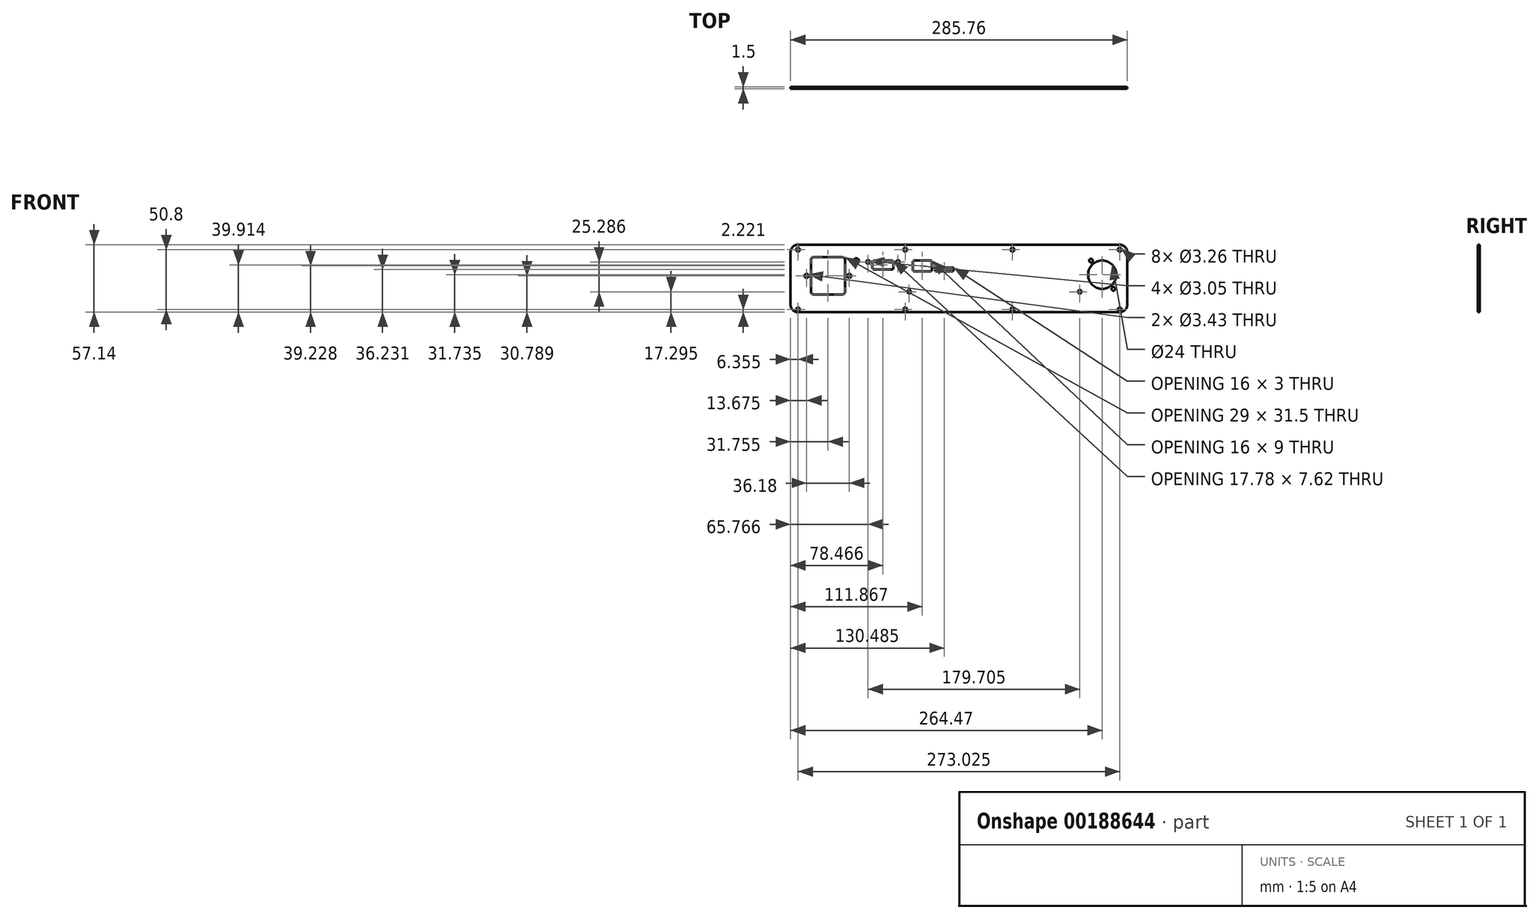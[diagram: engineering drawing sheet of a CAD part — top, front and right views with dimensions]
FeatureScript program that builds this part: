
annotation { "Feature Type Name" : "Feature", "Feature Type Description" : "" }
export const myFeature = defineFeature(function(context is Context, id is Id, definition is map)
    precondition{}
    {
        {
            var Q0;
            Q0=qCreatedBy(makeId("Front.planeOp"),FACE);
            var sketch = newSketch(context, id + "F0", { "sketchPlane" : qUnion([Q0])});
            skLineSegment(sketch, "E0", {"start": v(136.53, 28.58) * mm, "end": v(-136.53, 28.58) * mm});
            skArc(sketch, "E1", {"start": v(-136.53, 28.58) * mm, "mid": v(-141.02, 26.72) * mm, "end": v(-142.88, 22.23) * mm});
            skLineSegment(sketch, "E2", {"start": v(-142.88, 22.23) * mm, "end": v(-142.88, -22.23) * mm});
            skArc(sketch, "E3", {"start": v(-142.88, -22.23) * mm, "mid": v(-141.02, -26.72) * mm, "end": v(-136.53, -28.58) * mm});
            skLineSegment(sketch, "E4", {"start": v(-136.53, -28.58) * mm, "end": v(136.53, -28.58) * mm});
            skArc(sketch, "E5", {"start": v(136.53, -28.58) * mm, "mid": v(141.02, -26.72) * mm, "end": v(142.88, -22.23) * mm});
            skLineSegment(sketch, "E6", {"start": v(142.88, -22.23) * mm, "end": v(142.88, 22.23) * mm});
            skArc(sketch, "E7", {"start": v(142.88, 22.23) * mm, "mid": v(141.02, 26.72) * mm, "end": v(136.53, 28.58) * mm});
            skCircle(sketch, "E8", {"center": v(-87.1, 14.8) * mm, "radius": 2.29 * mm});
            skCircle(sketch, "E9", {"center": v(-42.19, -11.28) * mm, "radius": 1.52 * mm});
            skCircle(sketch, "E10", {"center": v(102.6, -11.28) * mm, "radius": 1.52 * mm});
            skLineSegment(sketch, "E11", {"start": v(-4.4, 8.27) * mm, "end": v(-4.4, 7.05) * mm});
            skArc(sketch, "E12", {"start": v(-5.28, 6.16) * mm, "mid": v(-4.66, 6.42) * mm, "end": v(-4.4, 7.05) * mm});
            skLineSegment(sketch, "E13", {"start": v(-5.28, 6.16) * mm, "end": v(-19.5, 6.16) * mm});
            skArc(sketch, "E14", {"start": v(-20.4, 7.05) * mm, "mid": v(-20.13, 6.42) * mm, "end": v(-19.5, 6.16) * mm});
            skLineSegment(sketch, "E15", {"start": v(-20.4, 7.05) * mm, "end": v(-20.4, 8.27) * mm});
            skArc(sketch, "E16", {"start": v(-19.5, 9.16) * mm, "mid": v(-20.13, 8.9) * mm, "end": v(-20.4, 8.27) * mm});
            skLineSegment(sketch, "E17", {"start": v(-19.5, 9.16) * mm, "end": v(-5.28, 9.16) * mm});
            skArc(sketch, "E18", {"start": v(-4.4, 8.27) * mm, "mid": v(-4.66, 8.9) * mm, "end": v(-5.28, 9.16) * mm});
            skCircle(sketch, "E19", {"center": v(-77.11, 14.01) * mm, "radius": 1.52 * mm});
            skCircle(sketch, "E20", {"center": v(-51.71, 14.01) * mm, "radius": 1.52 * mm});
            skCircle(sketch, "E21", {"center": v(121.6, 3.17) * mm, "radius": 12 * mm});
            skCircle(sketch, "E22", {"center": v(112.12, 15.15) * mm, "radius": 1.55 * mm});
            skCircle(sketch, "E23", {"center": v(131.12, -8.85) * mm, "radius": 1.55 * mm});
            skCircle(sketch, "E24", {"center": v(-129.2, 2.22) * mm, "radius": 1.71 * mm});
            skLineSegment(sketch, "E25", {"start": v(-96.62, 15.97) * mm, "end": v(-96.62, -11.53) * mm});
            skArc(sketch, "E26", {"start": v(-98.62, -13.53) * mm, "mid": v(-97.21, -12.95) * mm, "end": v(-96.62, -11.53) * mm});
            skLineSegment(sketch, "E27", {"start": v(-98.62, -13.53) * mm, "end": v(-123.63, -13.53) * mm});
            skArc(sketch, "E28", {"start": v(-125.63, -11.53) * mm, "mid": v(-125.04, -12.95) * mm, "end": v(-123.63, -13.53) * mm});
            skLineSegment(sketch, "E29", {"start": v(-125.63, -11.53) * mm, "end": v(-125.63, 15.97) * mm});
            skArc(sketch, "E30", {"start": v(-123.63, 17.97) * mm, "mid": v(-125.04, 17.38) * mm, "end": v(-125.63, 15.97) * mm});
            skLineSegment(sketch, "E31", {"start": v(-123.63, 17.97) * mm, "end": v(-98.62, 17.97) * mm});
            skArc(sketch, "E32", {"start": v(-96.62, 15.97) * mm, "mid": v(-97.21, 17.38) * mm, "end": v(-98.62, 17.97) * mm});
            skCircle(sketch, "E33", {"center": v(-93.02, 2.22) * mm, "radius": 1.71 * mm});
            skCircle(sketch, "E34", {"center": v(-136.53, 24.45) * mm, "radius": 1.63 * mm});
            skCircle(sketch, "E35", {"center": v(-136.53, -26.35) * mm, "radius": 1.63 * mm});
            skCircle(sketch, "E36", {"center": v(-45.52, 24.45) * mm, "radius": 1.63 * mm});
            skCircle(sketch, "E37", {"center": v(-45.52, -26.35) * mm, "radius": 1.63 * mm});
            skCircle(sketch, "E38", {"center": v(45.5, 24.45) * mm, "radius": 1.63 * mm});
            skCircle(sketch, "E39", {"center": v(45.5, -26.35) * mm, "radius": 1.63 * mm});
            skCircle(sketch, "E40", {"center": v(136.5, 24.45) * mm, "radius": 1.63 * mm});
            skCircle(sketch, "E41", {"center": v(136.5, -26.35) * mm, "radius": 1.63 * mm});
            skPoint(sketch, "E42", {"position": v(-73.3, 15.15) * mm});
            skPoint(sketch, "E43", {"position": v(-55.52, 7.53) * mm});
            skLineSegment(sketch, "E44.bottom", {"start": v(-71.8, 15.15) * mm, "end": v(-57.02, 15.15) * mm});
            skLineSegment(sketch, "E44.top", {"start": v(-71.8, 7.53) * mm, "end": v(-57.02, 7.53) * mm});
            skLineSegment(sketch, "E44.left", {"start": v(-73.3, 13.65) * mm, "end": v(-73.3, 9.03) * mm});
            skLineSegment(sketch, "E44.right", {"start": v(-55.52, 13.65) * mm, "end": v(-55.52, 9.03) * mm});
            skPoint(sketch, "E45", {"position": v(-142.88, -28.58) * mm});
            skArc(sketch, "E46.filletArc", {"start": v(-71.8, 15.15) * mm, "mid": v(-72.86, 14.71) * mm, "end": v(-73.3, 13.65) * mm});
            skPoint(sketch, "E47.visualSharp", {"position": v(-55.52, 15.15) * mm});
            skArc(sketch, "E47.filletArc", {"start": v(-55.52, 13.65) * mm, "mid": v(-55.96, 14.71) * mm, "end": v(-57.02, 15.15) * mm});
            skArc(sketch, "E48.filletArc", {"start": v(-57.02, 7.53) * mm, "mid": v(-55.96, 7.97) * mm, "end": v(-55.52, 9.03) * mm});
            skPoint(sketch, "E49.visualSharp", {"position": v(-73.3, 7.53) * mm});
            skArc(sketch, "E49.filletArc", {"start": v(-73.3, 9.03) * mm, "mid": v(-72.86, 7.97) * mm, "end": v(-71.8, 7.53) * mm});
            skPoint(sketch, "E50", {"position": v(-39.01, 15.16) * mm});
            skPoint(sketch, "E51", {"position": v(-23.01, 6.16) * mm});
            skLineSegment(sketch, "E52.bottom", {"start": v(-38.12, 15.16) * mm, "end": v(-23.9, 15.16) * mm});
            skLineSegment(sketch, "E52.top", {"start": v(-38.12, 6.16) * mm, "end": v(-23.9, 6.16) * mm});
            skLineSegment(sketch, "E52.left", {"start": v(-39.01, 14.27) * mm, "end": v(-39.01, 7.05) * mm});
            skLineSegment(sketch, "E52.right", {"start": v(-23.01, 14.27) * mm, "end": v(-23.01, 7.05) * mm});
            skArc(sketch, "E53.filletArc", {"start": v(-38.12, 15.16) * mm, "mid": v(-38.75, 14.9) * mm, "end": v(-39.01, 14.27) * mm});
            skPoint(sketch, "E54.visualSharp", {"position": v(-23.01, 15.16) * mm});
            skArc(sketch, "E54.filletArc", {"start": v(-23.01, 14.27) * mm, "mid": v(-23.27, 14.9) * mm, "end": v(-23.9, 15.16) * mm});
            skArc(sketch, "E55.filletArc", {"start": v(-23.9, 6.16) * mm, "mid": v(-23.27, 6.42) * mm, "end": v(-23.01, 7.05) * mm});
            skPoint(sketch, "E56.visualSharp", {"position": v(-39.01, 6.16) * mm});
            skArc(sketch, "E56.filletArc", {"start": v(-39.01, 7.05) * mm, "mid": v(-38.75, 6.42) * mm, "end": v(-38.12, 6.16) * mm});
            skSolve(sketch);
        }
        {
            var Q0;
            Q0=makeQuery(id+"F0.imprint","IMPRINT",FACE,{"disambiguationData":[TD([[makeQuery(id+"F0.imprint","IMPRINT",EDGE,{"derivedFrom":sQuery(id+"F0.wireOp",EDGE,"E0")}),1.0]])]});
            extrude(context, id + "F1", {"entities" : qUnion([Q0]), "depth" : 1.5 * mm});
        }
    });
